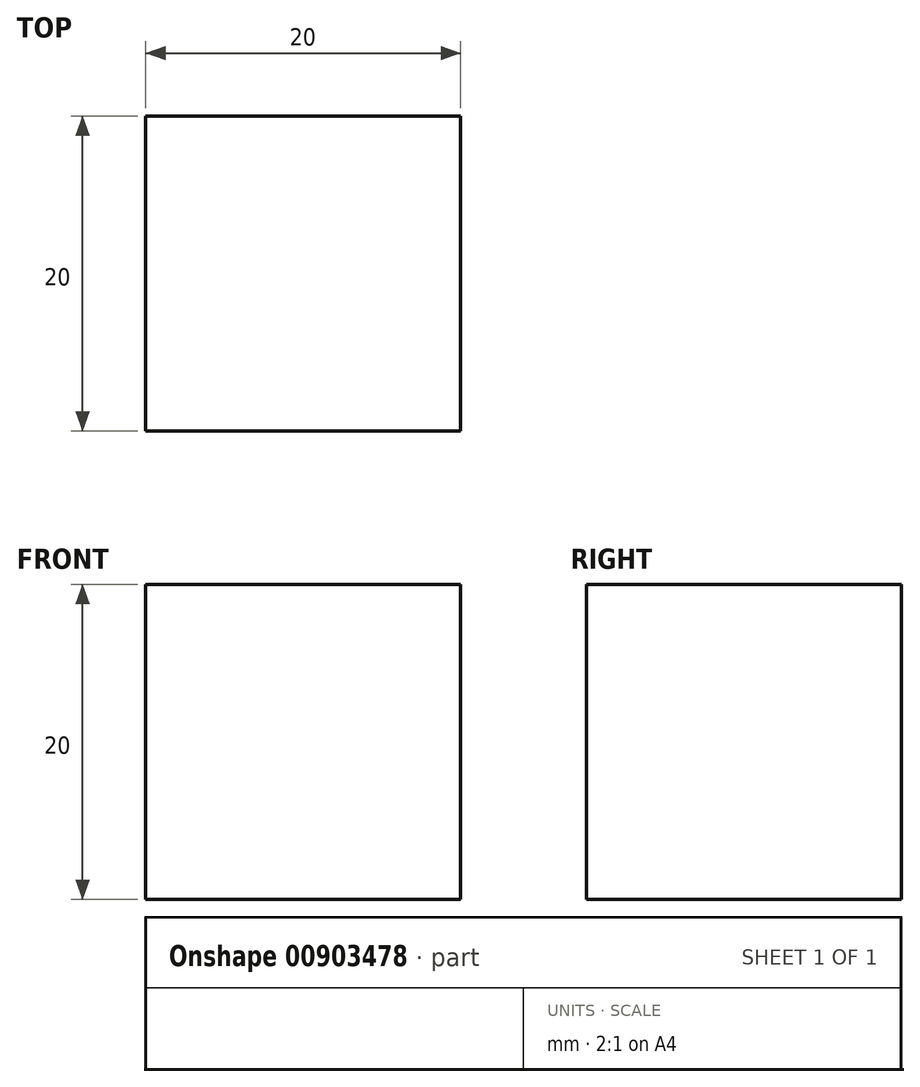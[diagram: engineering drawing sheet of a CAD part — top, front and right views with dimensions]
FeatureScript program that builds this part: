
annotation { "Feature Type Name" : "Feature", "Feature Type Description" : "" }
export const myFeature = defineFeature(function(context is Context, id is Id, definition is map)
    precondition{}
    {
        {
            var Q0;
            Q0=qCreatedBy(makeId("Top.planeOp"), FACE);
            var sketch = newSketch(context, id + "F0", { "sketchPlane" : qUnion([Q0])});
            skLineSegment(sketch, "E0.bottom", {"start": v(10, -10) * mm, "end": v(-10, -10) * mm});
            skLineSegment(sketch, "E0.top", {"start": v(10, 10) * mm, "end": v(-10, 10) * mm});
            skLineSegment(sketch, "E0.left", {"start": v(10, -10) * mm, "end": v(10, 10) * mm});
            skLineSegment(sketch, "E0.right", {"start": v(-10, -10) * mm, "end": v(-10, 10) * mm});
            skPoint(sketch, "E0.middle", {"position": v(0, 0) * mm});
            skSolve(sketch);
        }
        {
            var Q0;
            Q0 = qSketchRegion(id + "F0", true);
            extrude(context, id + "F1", {"entities" : qUnion([Q0]), "depth" : 20 * mm, "offsetDistance" : 25 * mm});
        }
    });
